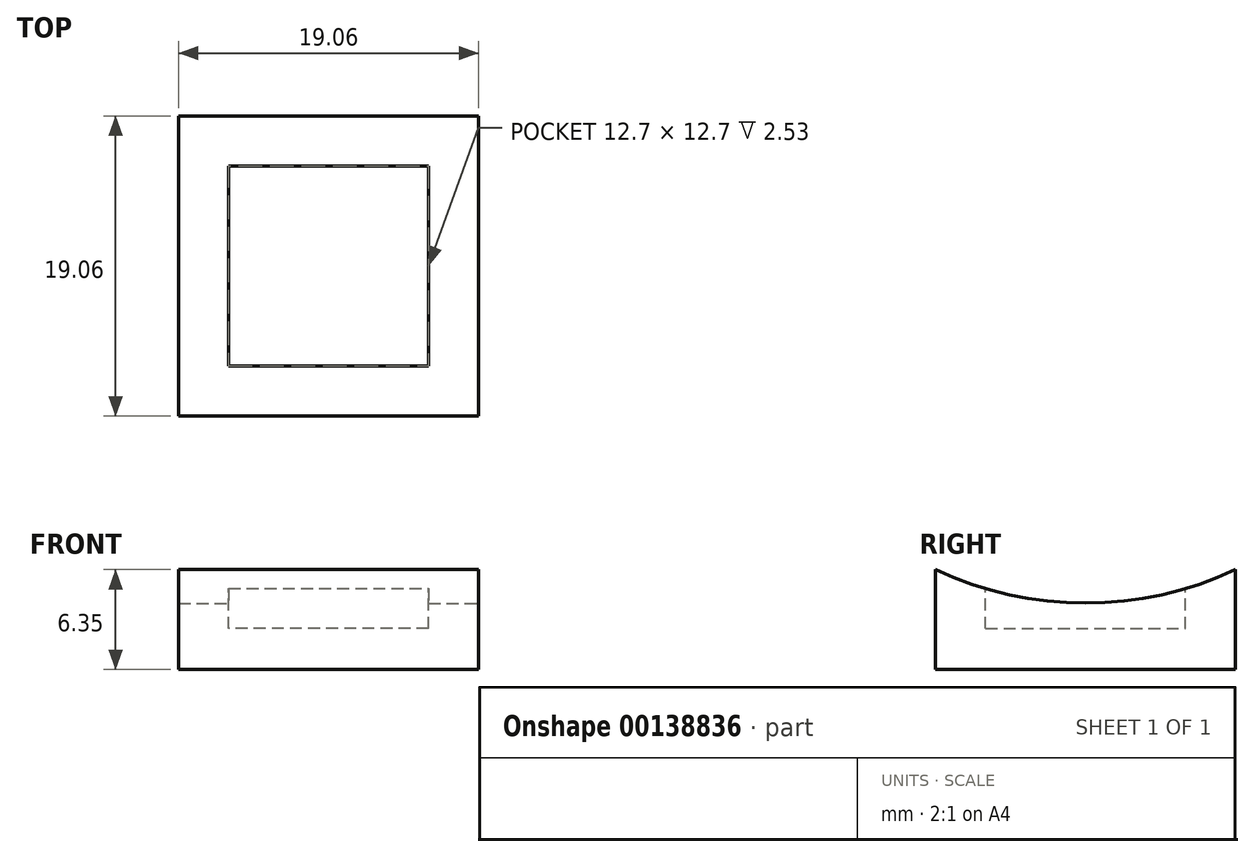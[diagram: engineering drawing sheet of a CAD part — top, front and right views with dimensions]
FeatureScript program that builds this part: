
annotation { "Feature Type Name" : "Feature", "Feature Type Description" : "" }
export const myFeature = defineFeature(function(context is Context, id is Id, definition is map)
    precondition{}
    {
        {
            var Q0;
            Q0=qCreatedBy(makeId("Top.planeOp"),FACE);
            var sketch = newSketch(context, id + "F0", { "sketchPlane" : qUnion([Q0])});
            skLineSegment(sketch, "E0.bottom", {"start": v(9.53, -9.52) * mm, "end": v(-9.52, -9.53) * mm});
            skLineSegment(sketch, "E0.top", {"start": v(9.52, 9.53) * mm, "end": v(-9.53, 9.53) * mm});
            skLineSegment(sketch, "E0.left", {"start": v(9.53, -9.52) * mm, "end": v(9.52, 9.53) * mm});
            skLineSegment(sketch, "E0.right", {"start": v(-9.52, -9.53) * mm, "end": v(-9.53, 9.53) * mm});
            skPoint(sketch, "E0.middle", {"position": v(0, 0) * mm});
            skSolve(sketch);
        }
        {
            var Q0;
            Q0=makeQuery(id+"F0.imprint","IMPRINT",FACE,{"disambiguationData":[TD([[makeQuery(id+"F0.imprint","IMPRINT",EDGE,{"derivedFrom":sQuery(id+"F0.wireOp",EDGE,"E0.bottom")}),-1.0]])]});
            extrude(context, id + "F1", {"entities" : qUnion([Q0]), "depth" : 6.35 * mm});
        }
        {
            var Q0;
            Q0=makeQuery(id+"F1.opExtrude","CAP_FACE",FACE,{"disambiguationData":[OSD([sQuery(id+"F0.wireOp",EDGE,"E0.bottom"),sQuery(id+"F0.wireOp",EDGE,"E0.top"),sQuery(id+"F0.wireOp",EDGE,"E0.left"),sQuery(id+"F0.wireOp",EDGE,"E0.right")])],"isStart":false});
            var sketch = newSketch(context, id + "F2", { "sketchPlane" : qUnion([Q0])});
            skLineSegment(sketch, "E1.bottom", {"start": v(6.35, -6.35) * mm, "end": v(-6.35, -6.35) * mm});
            skLineSegment(sketch, "E1.top", {"start": v(6.35, 6.35) * mm, "end": v(-6.35, 6.35) * mm});
            skLineSegment(sketch, "E1.left", {"start": v(6.35, -6.35) * mm, "end": v(6.35, 6.35) * mm});
            skLineSegment(sketch, "E1.right", {"start": v(-6.35, -6.35) * mm, "end": v(-6.35, 6.35) * mm});
            skPoint(sketch, "E1.middle", {"position": v(0, 0) * mm});
            skSolve(sketch);
        }
        {
            var Q0;
            Q0=makeQuery(id+"F2.imprint","IMPRINT",FACE,{"disambiguationData":[TD([[makeQuery(id+"F2.imprint","IMPRINT",EDGE,{"derivedFrom":sQuery(id+"F2.wireOp",EDGE,"E1.bottom")}),-1.0]])]});
            extrude(context, id + "F3", {"entities" : qUnion([Q0]), "operationType" : NewBodyOperationType.REMOVE, "oppositeDirection" : true, "depth" : 3.74 * mm});
        }
        {
            var Q0;
            Q0=makeQuery(id+"F1.opExtrude","SWEPT_FACE",FACE,{"disambiguationData":[OSD([sQuery(id+"F0.wireOp",EDGE,"E0.left")])]});
            var sketch = newSketch(context, id + "F4", { "sketchPlane" : qUnion([Q0])});
            skArc(sketch, "E2", {"start": v(-9.53, 6.35) * mm, "mid": v(0, 4.21) * mm, "end": v(9.53, 6.35) * mm});
            skSolve(sketch);
        }
        {
            var Q0;
            Q0=makeQuery(id+"F4.imprint","IMPRINT",FACE,{"disambiguationData":[TD([[makeQuery(id+"F4.imprint","IMPRINT",EDGE,{"derivedFrom":sQuery(id+"F4.wireOp",EDGE,"E2")}),1.0]])]});
            extrude(context, id + "F5", {"entities" : qUnion([Q0]), "operationType" : NewBodyOperationType.REMOVE, "oppositeDirection" : true, "depth" : 25.4 * mm});
        }
    });
